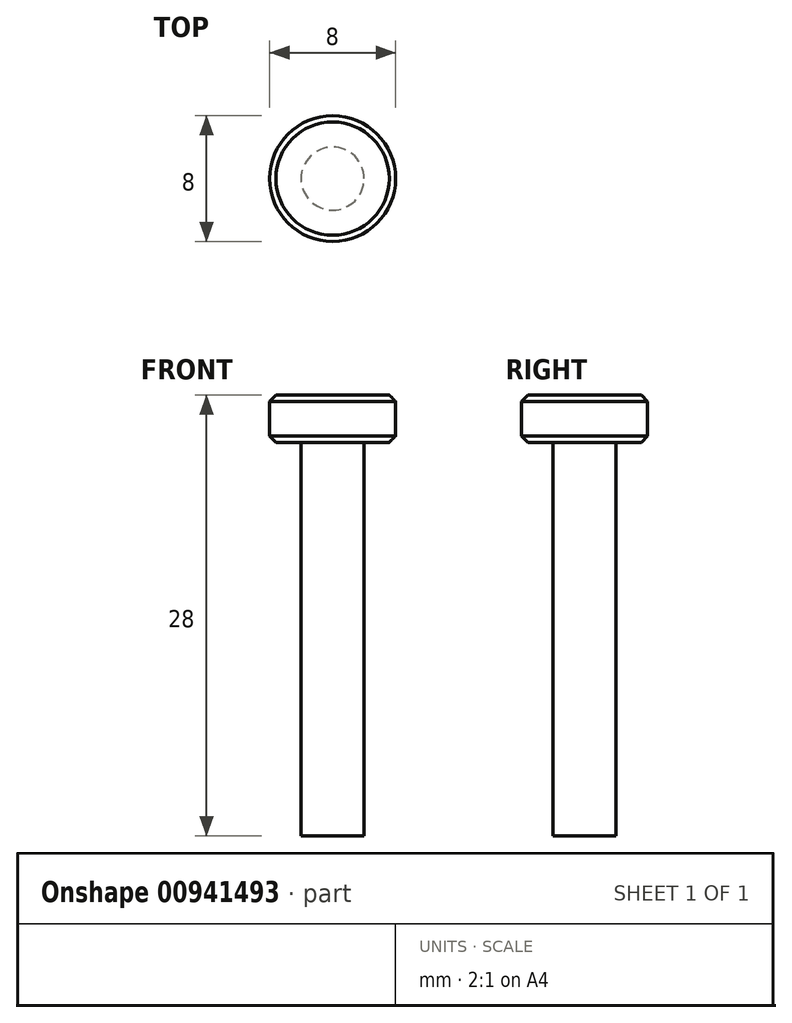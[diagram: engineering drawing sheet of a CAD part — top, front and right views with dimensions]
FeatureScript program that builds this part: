
annotation { "Feature Type Name" : "Feature", "Feature Type Description" : "" }
export const myFeature = defineFeature(function(context is Context, id is Id, definition is map)
    precondition{}
    {
        {
            var Q0;
            Q0=qCreatedBy(makeId("Top.planeOp"),FACE);
            var sketch = newSketch(context, id + "F0", { "sketchPlane" : qUnion([Q0])});
            skCircle(sketch, "E0", {"center": v(0, 0) * mm, "radius": 2 * mm});
            skSolve(sketch);
        }
        {
            var Q0;
            Q0=makeQuery(id+"F0.imprint","IMPRINT",FACE,{"disambiguationData":[TD([[makeQuery(id+"F0.imprint","IMPRINT",EDGE,{"derivedFrom":sQuery(id+"F0.wireOp",EDGE,"E0")}),1.0]])]});
            extrude(context, id + "F1", {"entities" : qUnion([Q0]), "depth" : 25 * mm, "offsetDistance" : 25 * mm});
        }
        {
            var Q0;
            Q0=makeQuery(id+"F1.opExtrude","CAP_FACE",FACE,{"disambiguationData":[OSD([sQuery(id+"F0.wireOp",EDGE,"E0")])],"isStart":false});
            var sketch = newSketch(context, id + "F2", { "sketchPlane" : qUnion([Q0])});
            skCircle(sketch, "E1", {"center": v(0, 0) * mm, "radius": 4 * mm});
            skSolve(sketch);
        }
        {
            var Q0;
            Q0=makeQuery(id+"F2.imprint","IMPRINT",FACE,{"disambiguationData":[TD([[makeQuery(id+"F2.imprint","IMPRINT",EDGE,{"derivedFrom":sQuery(id+"F2.wireOp",EDGE,"E1")}),1.0]])]});
            var Q1;
            Q1=makeQuery(id+"F2.imprint","IMPRINT",FACE,{"disambiguationData":[TD([[makeQuery(id+"F2.imprint","IMPRINT",EDGE,{"derivedFrom":makeQuery(id+"F1.opExtrude","CAP_EDGE",EDGE,{"disambiguationData":[OSD([sQuery(id+"F0.wireOp",EDGE,"E0")])],"isStart":false})}),1.0]])]});
            extrude(context, id + "F3", {"entities" : qUnion([Q0, Q1]), "operationType" : NewBodyOperationType.ADD, "depth" : 3 * mm, "offsetDistance" : 25 * mm});
        }
        {
            var Q0;
            Q0=makeQuery(id+"F3.opExtrude","CAP_EDGE",EDGE,{"disambiguationData":[OSD([sQuery(id+"F2.wireOp",EDGE,"E1")])],"isStart":false});
            var Q1;
            Q1=makeQuery(id+"F3.opExtrude","CAP_EDGE",EDGE,{"disambiguationData":[OSD([sQuery(id+"F2.wireOp",EDGE,"E1")])],"isStart":true});
            chamfer(context, id + "F4", {"entities" : qUnion([Q0, Q1]), "width" : 0.4 * mm, "tangentPropagation" : true});
        }
    });
